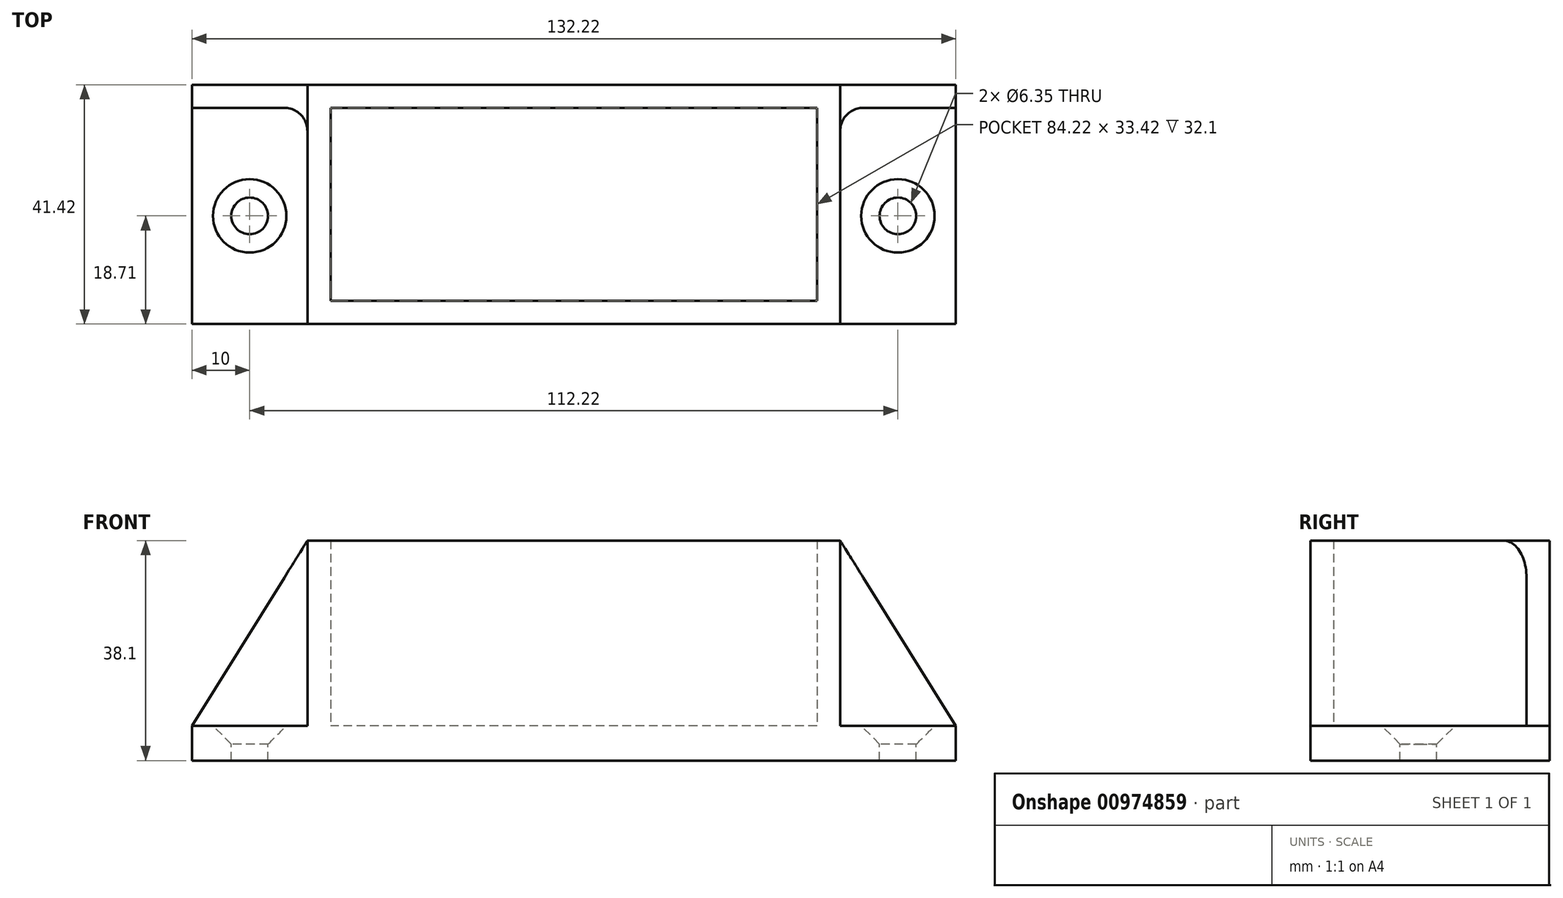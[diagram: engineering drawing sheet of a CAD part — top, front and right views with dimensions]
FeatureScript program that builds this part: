
annotation { "Feature Type Name" : "Feature", "Feature Type Description" : "" }
export const myFeature = defineFeature(function(context is Context, id is Id, definition is map)
    precondition{}
    {
        {
            var Q0;
            Q0=qCreatedBy(makeId("Top.planeOp"),FACE);
            var sketch = newSketch(context, id + "F0", { "sketchPlane" : qUnion([Q0])});
            skLineSegment(sketch, "E0.bottom", {"start": v(42.1, 16.71) * mm, "end": v(-42.1, 16.71) * mm});
            skLineSegment(sketch, "E0.top", {"start": v(42.1, -16.71) * mm, "end": v(-42.1, -16.71) * mm});
            skLineSegment(sketch, "E0.left", {"start": v(42.1, 16.71) * mm, "end": v(42.1, -16.71) * mm});
            skLineSegment(sketch, "E0.right", {"start": v(-42.1, 16.71) * mm, "end": v(-42.1, -16.71) * mm});
            skPoint(sketch, "E0.middle", {"position": v(0, 0) * mm});
            skLineSegment(sketch, "E1.0", {"start": v(46.1, 20.71) * mm, "end": v(-46.1, 20.71) * mm});
            skLineSegment(sketch, "E1.1", {"start": v(46.1, 20.71) * mm, "end": v(46.1, -20.71) * mm});
            skLineSegment(sketch, "E1.2", {"start": v(46.1, -20.71) * mm, "end": v(-46.1, -20.71) * mm});
            skLineSegment(sketch, "E1.3", {"start": v(-46.1, 20.71) * mm, "end": v(-46.1, -20.71) * mm});
            skLineSegment(sketch, "E2.bottom", {"start": v(-46.1, 20.71) * mm, "end": v(-66.11, 20.71) * mm});
            skLineSegment(sketch, "E2.top", {"start": v(-46.1, -20.71) * mm, "end": v(-66.11, -20.71) * mm});
            skLineSegment(sketch, "E2.right", {"start": v(-66.11, 20.71) * mm, "end": v(-66.11, -20.71) * mm});
            skLineSegment(sketch, "E3", {"start": v(-46.1, 16.71) * mm, "end": v(-66.11, 16.71) * mm});
            skLineSegment(sketch, "E4", {"start": v(0, 0) * mm, "end": v(0, 5.6) * mm, "construction": true});
            skLineSegment(sketch, "E5.MirrorCS", {"start": v(46.1, 20.71) * mm, "end": v(66.11, 20.71) * mm});
            skLineSegment(sketch, "E6.MirrorCS", {"start": v(46.1, 16.71) * mm, "end": v(66.11, 16.71) * mm});
            skLineSegment(sketch, "E7.MirrorCS", {"start": v(66.11, 20.71) * mm, "end": v(66.11, -20.71) * mm});
            skLineSegment(sketch, "E8.MirrorCS", {"start": v(46.1, -20.71) * mm, "end": v(66.11, -20.71) * mm});
            skSolve(sketch);
        }
        {
            var Q0;
            Q0=makeQuery(id+"F0.imprint","IMPRINT",FACE,{"disambiguationData":[TD([[makeQuery(id+"F0.imprint","IMPRINT",EDGE,{"derivedFrom":sQuery(id+"F0.wireOp",EDGE,"E0.bottom")}),-1.0]])]});
            var Q1;
            {var subQ0=sQuery(id+"F0.wireOp",EDGE,"E5.MirrorCS");Q1=makeQuery(id+"F0.imprint","IMPRINT",FACE,{"disambiguationData":[TD([[makeQuery(id+"F0.imprint","IMPRINT",EDGE,{"derivedFrom":subQ0}),-1.0]])]});}
            var Q2;
            {var subQ0=sQuery(id+"F0.wireOp",EDGE,"E2.bottom");Q2=makeQuery(id+"F0.imprint","IMPRINT",FACE,{"disambiguationData":[TD([[makeQuery(id+"F0.imprint","IMPRINT",EDGE,{"derivedFrom":subQ0}),1.0]])]});}
            extrude(context, id + "F1", {"entities" : qUnion([Q0, Q1, Q2]), "depth" : 38.1 * mm, "offsetDistance" : 25 * mm});
        }
        {
            var Q0;
            {var subQ0=sQuery(id+"F0.wireOp",EDGE,"E2.top");Q0=makeQuery(id+"F0.imprint","IMPRINT",FACE,{"disambiguationData":[TD([[makeQuery(id+"F0.imprint","IMPRINT",EDGE,{"derivedFrom":subQ0}),-1.0]])]});}
            var Q1;
            {var subQ2=sQuery(id+"F0.wireOp",EDGE,"E6.MirrorCS");Q1=makeQuery(id+"F0.imprint","IMPRINT",FACE,{"disambiguationData":[TD([[makeQuery(id+"F0.imprint","IMPRINT",EDGE,{"derivedFrom":subQ2}),-1.0]])]});}
            var Q2;
            Q2=makeQuery(id+"F0.imprint","IMPRINT",FACE,{"disambiguationData":[TD([[makeQuery(id+"F0.imprint","IMPRINT",EDGE,{"derivedFrom":sQuery(id+"F0.wireOp",EDGE,"E0.bottom")}),1.0]])]});
            extrude(context, id + "F2", {"entities" : qUnion([Q0, Q1, Q2]), "operationType" : NewBodyOperationType.ADD, "depth" : 6 * mm, "offsetDistance" : 25 * mm});
        }
        {
            var Q0;
            Q0=makeQuery(id+"F2.opExtrude","CAP_FACE",FACE,{"disambiguationData":[OSD([sQuery(id+"F0.wireOp",EDGE,"E2.top"),sQuery(id+"F0.wireOp",EDGE,"E1.3"),sQuery(id+"F0.wireOp",EDGE,"E2.right"),sQuery(id+"F0.wireOp",EDGE,"E3")])],"isStart":false});
            var sketch = newSketch(context, id + "F3", { "sketchPlane" : qUnion([Q0])});
            skLineSegment(sketch, "E9", {"start": v(-46.1, 16.71) * mm, "end": v(-66.11, -20.71) * mm, "construction": true});
            skPoint(sketch, "E10", {"position": v(-56.1, -2) * mm});
            skLineSegment(sketch, "E11.MirrorCS", {"start": v(46.1, 16.71) * mm, "end": v(66.11, -20.71) * mm, "construction": true});
            skPoint(sketch, "E12.MirrorP", {"position": v(56.1, -2) * mm});
            skSolve(sketch);
        }
        {
            var Q0;
            Q0=sQuery(id+"F3.wireOp",VERTEX,"E10");
            var Q1;
            Q1=sQuery(id+"F3.wireOp",VERTEX,"E12.MirrorP");
            var Q2;
            Q2=makeQuery(id+"F1.opExtrude","SWEPT_BODY",BODY,{"disambiguationData":[OSD([sQuery(id+"F0.wireOp",EDGE,"E0.bottom"),sQuery(id+"F0.wireOp",EDGE,"E0.top"),sQuery(id+"F0.wireOp",EDGE,"E0.left"),sQuery(id+"F0.wireOp",EDGE,"E0.right"),sQuery(id+"F0.wireOp",EDGE,"E1.0"),sQuery(id+"F0.wireOp",EDGE,"E1.1"),sQuery(id+"F0.wireOp",EDGE,"E1.2"),sQuery(id+"F0.wireOp",EDGE,"E2.bottom"),sQuery(id+"F0.wireOp",EDGE,"E1.3"),sQuery(id+"F0.wireOp",EDGE,"E2.right"),sQuery(id+"F0.wireOp",EDGE,"E3"),sQuery(id+"F0.wireOp",EDGE,"E5.MirrorCS"),sQuery(id+"F0.wireOp",EDGE,"E6.MirrorCS"),sQuery(id+"F0.wireOp",EDGE,"E7.MirrorCS")])]});
            hole(context, id + "F4", {"style" : HoleStyle.C_SINK, "endStyle" : HoleEndStyle.THROUGH, "holeDiameter" : 6.35 * mm, "cSinkDiameter" : 12.7 * mm, "cSinkAngle" : 90 * degree, "majorDiameter" : 5 * mm, "isTappedThrough" : true, "tappedDepth" : 12 * mm, "tapClearance" : 3, "locations" : qUnion([Q0, Q1]), "scope" : qUnion([Q2])});
        }
        {
            var Q0;
            Q0=makeQuery(id+"F1.opExtrude","SWEPT_FACE",FACE,{"disambiguationData":[OSD([sQuery(id+"F0.wireOp",EDGE,"E1.0"),sQuery(id+"F0.wireOp",EDGE,"E2.bottom"),sQuery(id+"F0.wireOp",EDGE,"E5.MirrorCS")])]});
            var sketch = newSketch(context, id + "F5", { "sketchPlane" : qUnion([Q0])});
            skLineSegment(sketch, "E13", {"start": v(46.1, 38.1) * mm, "end": v(66.11, 6) * mm});
            skLineSegment(sketch, "E14", {"start": v(-46.1, 38.1) * mm, "end": v(-66.11, 6) * mm});
            skSolve(sketch);
        }
        {
            var Q0;
            {var subQ0=sQuery(id+"F5.wireOp",EDGE,"E14");Q0=makeQuery(id+"F5.imprint","IMPRINT",FACE,{"disambiguationData":[TD([[makeQuery(id+"F5.imprint","IMPRINT",EDGE,{"derivedFrom":subQ0}),-1.0]])]});}
            var Q1;
            {var subQ0=sQuery(id+"F5.wireOp",EDGE,"E13");Q1=makeQuery(id+"F5.imprint","IMPRINT",FACE,{"disambiguationData":[TD([[makeQuery(id+"F5.imprint","IMPRINT",EDGE,{"derivedFrom":subQ0}),1.0]])]});}
            extrude(context, id + "F6", {"entities" : qUnion([Q0, Q1]), "operationType" : NewBodyOperationType.REMOVE, "oppositeDirection" : true, "depth" : 25 * mm, "offsetDistance" : 25 * mm});
        }
        {
            var Q0;
            Q0=makeQuery(id+"F1.opExtrude","SWEPT_EDGE",EDGE,{"disambiguationData":[OSD([sQuery(id+"F0.wireOp",EDGE,"E1.1"),sQuery(id+"F0.wireOp",EDGE,"E6.MirrorCS")])]});
            var Q1;
            Q1=makeQuery(id+"F1.opExtrude","SWEPT_EDGE",EDGE,{"disambiguationData":[OSD([sQuery(id+"F0.wireOp",EDGE,"E1.3"),sQuery(id+"F0.wireOp",EDGE,"E3")])]});
            var Q2;
            Q2=makeQuery(id+"F2.opExtrude","CAP_EDGE",EDGE,{"disambiguationData":[OSD([sQuery(id+"F0.wireOp",EDGE,"E1.3")])],"isStart":false});
            var Q3;
            Q3=makeQuery(id+"F2.opExtrude","CAP_EDGE",EDGE,{"disambiguationData":[OSD([sQuery(id+"F0.wireOp",EDGE,"E3")])],"isStart":false});
            var Q4;
            Q4=makeQuery(id+"F2.opExtrude","CAP_EDGE",EDGE,{"disambiguationData":[OSD([sQuery(id+"F0.wireOp",EDGE,"E1.1")])],"isStart":false});
            var Q5;
            Q5=makeQuery(id+"F2.opExtrude","CAP_EDGE",EDGE,{"disambiguationData":[OSD([sQuery(id+"F0.wireOp",EDGE,"E6.MirrorCS")])],"isStart":false});
            fillet(context, id + "F7", {"entities" : qUnion([Q0, Q1, Q2, Q3, Q4, Q5]), "radius" : 4 * mm, "tangentPropagation" : true, "allowEdgeOverflow" : false});
        }
    });
